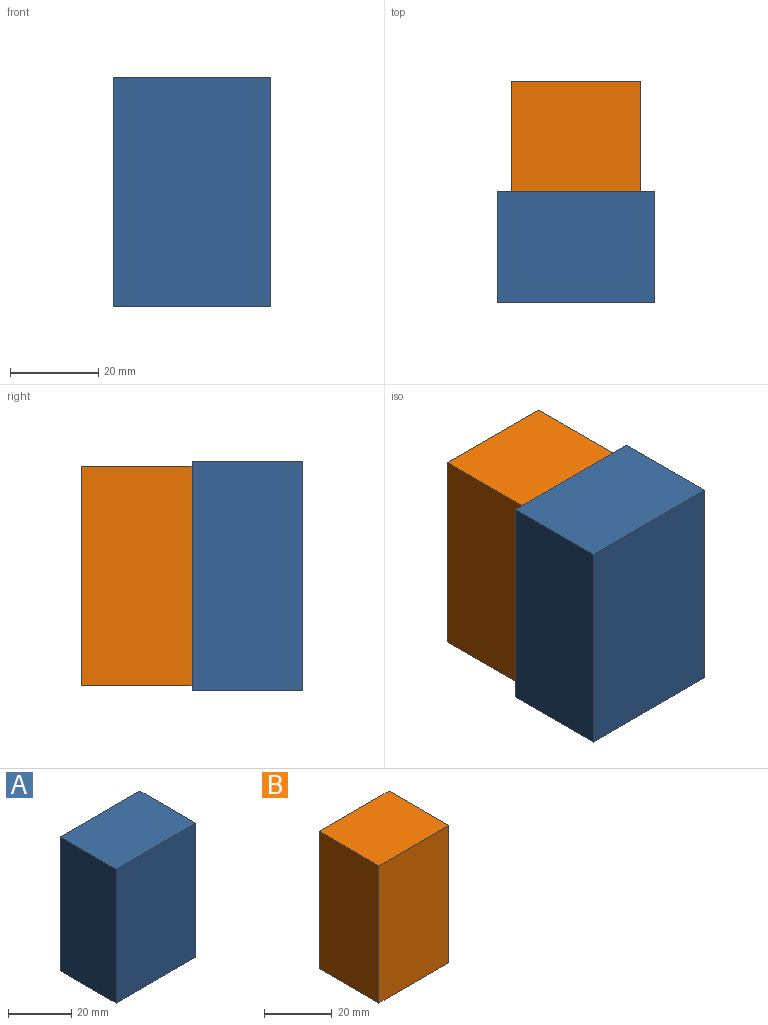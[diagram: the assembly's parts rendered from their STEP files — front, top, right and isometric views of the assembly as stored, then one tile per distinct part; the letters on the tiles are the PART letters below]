
ASSEMBLY  parts=2 mates=1
PART A: 6 faces, bbox 35.7x25x52 mm
  f0: plane 35.72x25mm, normal (0,0,1), area 892.9mm2, adj f1,f3,f4,f5
  f1: plane 51.97x25mm, normal (-1,0,0), area 1299.3mm2, adj f0,f2,f4,f5
  f2: plane 35.72x25mm, normal (0,0,-1), area 892.9mm2, adj f1,f3,f4,f5
  f3: plane 51.97x25mm, normal (1,0,0), area 1299.3mm2, adj f0,f2,f4,f5
  f4: plane 51.97x35.72mm, normal (0,-1,0), area 1856.2mm2, adj f0,f1,f2,f3
  f5: plane 51.97x35.72mm, normal (0,1,0), area 1856.2mm2, adj f0,f1,f2,f3
PART B: 6 faces, bbox 29.2x25x49.7 mm
  f0: plane 29.23x25mm, normal (0,0,1), area 730.7mm2, adj f1,f3,f4,f5
  f1: plane 49.73x25mm, normal (-1,0,0), area 1243.2mm2, adj f0,f2,f4,f5
  f2: plane 29.23x25mm, normal (0,0,-1), area 730.7mm2, adj f1,f3,f4,f5
  f3: plane 49.73x25mm, normal (1,0,0), area 1243.2mm2, adj f0,f2,f4,f5
  f4: plane 49.73x29.23mm, normal (0,-1,0), area 1453.5mm2, adj f0,f1,f2,f3
  f5: plane 49.73x29.23mm, normal (0,1,0), area 1453.5mm2, adj f0,f1,f2,f3
PLACE A rot(axis=(1,0,0),180deg) t=(72.94,-50,15.05)mm
PLACE B at identity
MATE revolute A.f4 <-> B.f4  axis (0,1,0) through (71.48,-25,7.7)mm
